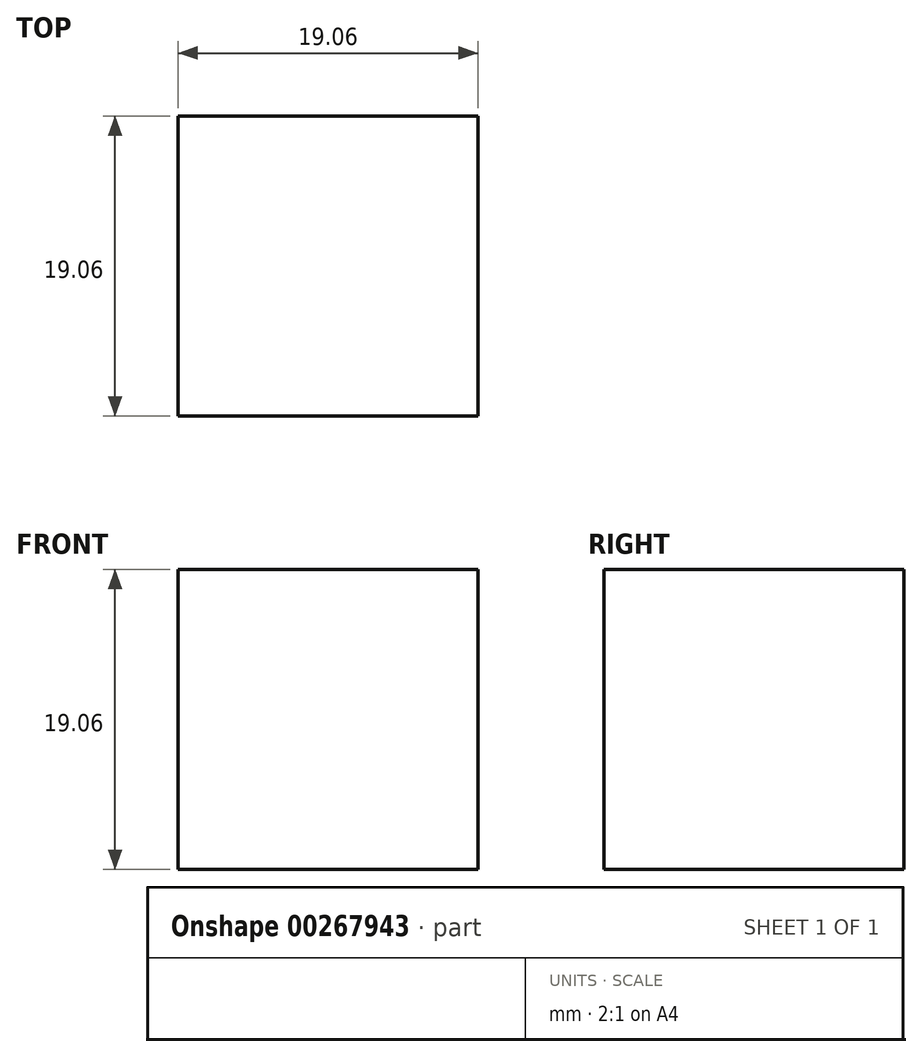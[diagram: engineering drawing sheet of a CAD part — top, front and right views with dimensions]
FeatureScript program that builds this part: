
annotation { "Feature Type Name" : "Feature", "Feature Type Description" : "" }
export const myFeature = defineFeature(function(context is Context, id is Id, definition is map)
    precondition{}
    {
        {
            var Q0;
            Q0=qCreatedBy(makeId("Front.planeOp"),FACE);
            var sketch = newSketch(context, id + "F0", { "sketchPlane" : qUnion([Q0])});
            skLineSegment(sketch, "E0.bottom", {"start": v(9.52, 9.52) * mm, "end": v(-9.52, 9.52) * mm});
            skLineSegment(sketch, "E0.top", {"start": v(9.52, -9.52) * mm, "end": v(-9.53, -9.52) * mm});
            skLineSegment(sketch, "E0.left", {"start": v(9.53, 9.52) * mm, "end": v(9.52, -9.52) * mm});
            skLineSegment(sketch, "E0.right", {"start": v(-9.53, 9.52) * mm, "end": v(-9.53, -9.52) * mm});
            skPoint(sketch, "E0.middle", {"position": v(0, 0) * mm});
            skSolve(sketch);
        }
        {
            var Q0;
            Q0 = qSketchRegion(id + "F0", true);
            extrude(context, id + "F1", {"entities" : qUnion([Q0]), "endBound" : BoundingType.SYMMETRIC, "depth" : 19.05 * mm});
        }
    });
